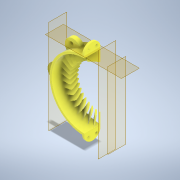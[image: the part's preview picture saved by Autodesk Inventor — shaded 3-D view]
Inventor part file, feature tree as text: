
AUTODESK INVENTOR PART (.ipt)
format: ipt  version: 2021.2 (Build 252289000, 289)  size: 1,526,272 bytes
history: native  units: in
note: dims shown in document units (in); Inventor stores cm internally (conversion verified against a paired STEP export)
features: sketch x11, extrude x10, plane x4, pattern_circular x3, fillet x2, loft x1, other x1
ambient origin geometry x8: Origin, YZ Plane, XZ Plane, XY Plane, X Axis, Y Axis, Z Axis, Center Point
bodies: Solid1 (feature_tree)
feature tree (32):
  extrude  "Extrusion1"  Depth=4.25in
  plane  "Work Plane1"
  plane  "Work Plane2"
  extrude  "Extrusion3"  Depth=1.5in
  fillet  "Fillet1"  Radius=2.125in
  extrude  "Extrusion4"  TaperAngle=0.0deg  [1 undecoded]
  pattern_circular  "Circular Pattern2"  Count=2 Angle=360.0deg
  plane  "Work Plane3"
  extrude  "Extrusion5"  Depth=1.0in
  extrude  "Extrusion6"  Depth=0.5in
  fillet  "Fillet2"  [1 undecoded]
  extrude  "Extrusion7"  Depth=0.5in TaperAngle=0.0deg
  pattern_circular  "Circular Pattern3"  [2 undecoded]
  extrude  "Extrusion8"  Depth=0.25in
  plane  "Work Plane4"
  loft  "Loft1"
  pattern_circular  "Circular Pattern5"  [2 undecoded]
  extrude  "Extrusion9"  Depth=2.3622in TaperAngle=360.0deg
  extrude  "Extrusion10"  Depth=0.25in
  extrude  "Extrusion11"  Depth=0.125in
  sketch  "Sketch1"  dims[d0=4.0in d1=4.25in]
  sketch  "Sketch3"  dims[d2=1.0in d3=0.0in d4=1.5in d10=2.125in]
  sketch  "Sketch4"  dims[d11=0.25in d12=0.0in]
  sketch  "Sketch5"  dims[d13=0.5in d14=0.0in]
  sketch  "Sketch6"  dims[d15=0.5in]
  sketch  "Sketch7"  dims[d16=0.125in]
  sketch  "Sketch8"  dims[d17=0.2in]
  sketch  "Sketch9"  dims[d18=0.5in d19=0.0in d20=0.7874in d21=360.0deg]
  other  "Edges1"
  sketch  "Sketch10"  dims[d23=-2.125in d24=1.0in]
  sketch  "Sketch11"  dims[d25=0.25in d26=0.5in d27=0.0in]
  sketch  "Sketch12"  dims[d28=0.1in d29=0.0in d30=0.5in d31=0.0in d32=0.5in d33=0.25in d34=0.2in d35=0.5in d36=0.0in d37=2.3622in d38=360.0deg d40=0.25in d41=0.125in d42=0.25in d43=0.2in d49=0.5in d50=0.0312in d51=0.5in d52=0.0in d56=0.9in d57=0.0in d58=90.0deg d59=0.0in d60=90.0deg d61=14.1732in d62=360.0deg d64=2.6625in d65=0.0in d66=0.0777in d67=0.0in d68=0.0in d69=0.8in d70=0.0in]
note: 6 required parameter values undecoded (feature->parameter linkage not recoverable at this tier; creation-order binding heuristic only, values carry confidence <= 0.55)
